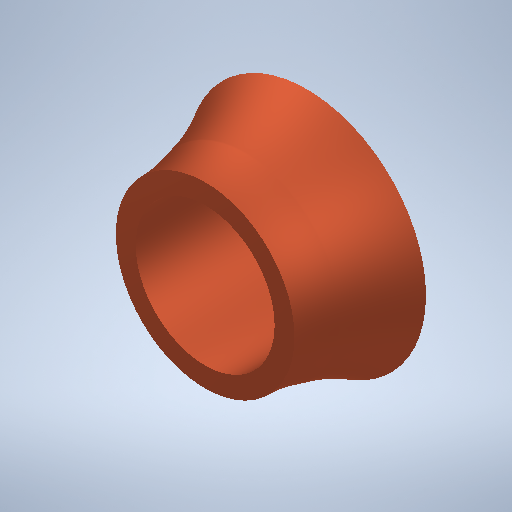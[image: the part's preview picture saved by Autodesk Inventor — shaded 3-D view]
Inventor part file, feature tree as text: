
AUTODESK INVENTOR PART (.ipt)
format: ipt  version: 2025 (Build 290162010, 162A)  size: 274,944 bytes
history: native  units: mm
features: sketch x2, revolve x1, hole x1, fillet x1
ambient origin geometry x8: Origin, YZ Plane, XZ Plane, XY Plane, X Axis, Y Axis, Z Axis, Center Point
bodies: Solid1 (feature_tree)
feature tree (5):
  revolve  "Revolution1"  [1 undecoded]
  hole  "Hole1"  [1 undecoded]
  fillet  "Fillet1"  Radius=10.0mm
  sketch  "Sketch1"  dims[d6=8.0mm d7=7.0mm]
  sketch  "Sketch2"  dims[d9=12.0mm d10=9.0mm d11=10.0mm d12=2.0mm d13=90.0deg d14=7.0mm d15=6.0mm d16=7.0mm d17=2.3mm d18=90.0deg d19=8.0mm d20=0.0mm d21=1.0mm]
note: 2 required parameter values undecoded (feature->parameter linkage not recoverable at this tier; creation-order binding heuristic only, values carry confidence <= 0.55)